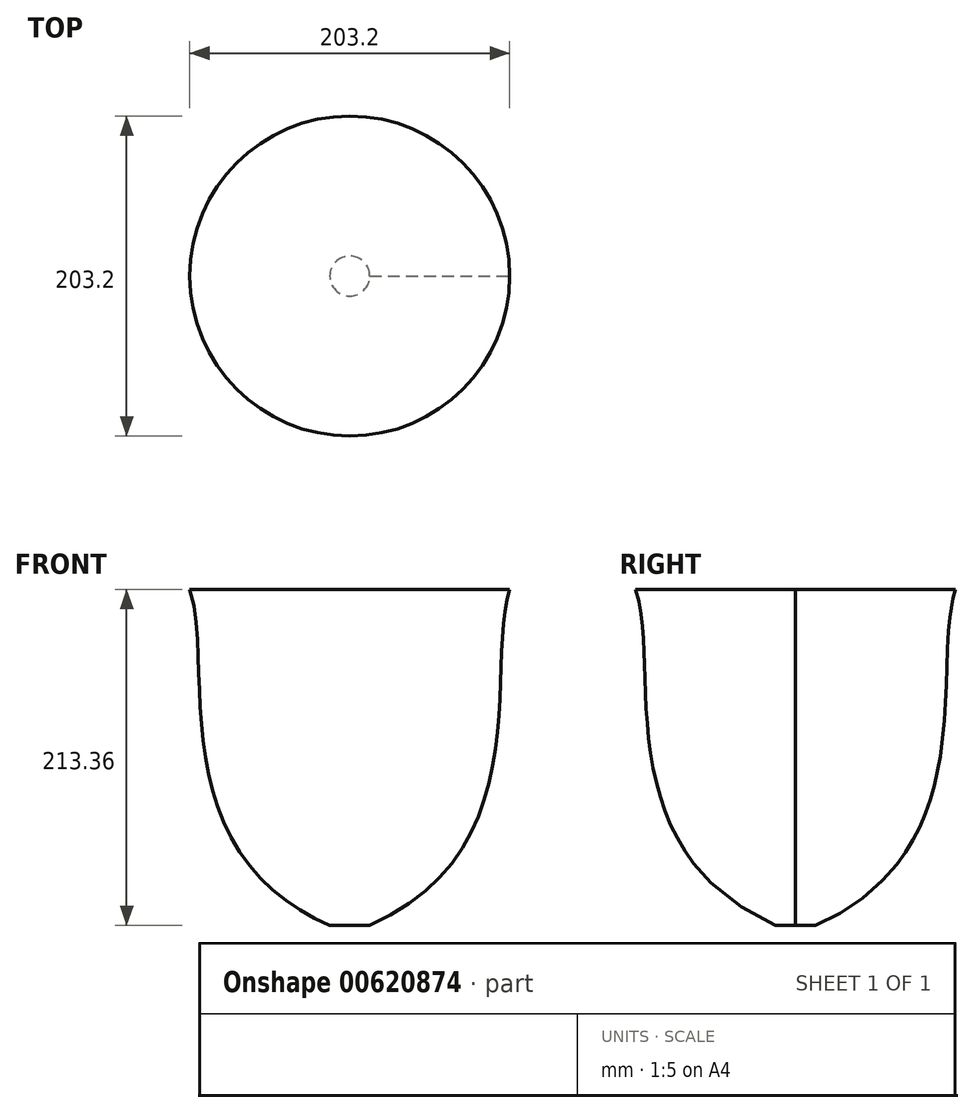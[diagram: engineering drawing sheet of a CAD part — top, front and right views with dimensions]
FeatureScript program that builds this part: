
annotation { "Feature Type Name" : "Feature", "Feature Type Description" : "" }
export const myFeature = defineFeature(function(context is Context, id is Id, definition is map)
    precondition{}
    {
        {
            var Q0;
            Q0=qCreatedBy(makeId("Front.planeOp"),FACE);
            var sketch = newSketch(context, id + "F0", { "sketchPlane" : qUnion([Q0])});
            skLineSegment(sketch, "E0.bottom", {"start": v(-101.6, 213.36) * mm, "end": v(101.6, 213.36) * mm, "construction": true});
            skLineSegment(sketch, "E0.top", {"start": v(-101.6, 0) * mm, "end": v(101.6, 0) * mm, "construction": true});
            skLineSegment(sketch, "E0.left", {"start": v(-101.6, 213.36) * mm, "end": v(-101.6, 0) * mm, "construction": true});
            skLineSegment(sketch, "E0.right", {"start": v(101.6, 213.36) * mm, "end": v(101.6, 0) * mm, "construction": true});
            skLineSegment(sketch, "E1", {"start": v(0, 33) * mm, "end": v(0, -35.39) * mm, "construction": true});
            skLineSegment(sketch, "E2", {"start": v(0, 0) * mm, "end": v(12.7, 0) * mm});
            skFitSpline(sketch, "E3", {"points": [v(12.7, 0) * mm, v(101.6, 213.36) * mm], "startDerivative": vector(324.37, 142.37) * mm, "endDerivative": vector(48.16, 142.84) * mm});
            skLineSegment(sketch, "E4", {"start": v(101.6, 213.36) * mm, "end": v(0, 213.36) * mm});
            skLineSegment(sketch, "E5", {"start": v(0, 213.36) * mm, "end": v(0, 0) * mm});
            skSolve(sketch);
        }
        {
            var Q0;
            Q0 = qSketchRegion(id + "F0", true);
            var Q1;
            Q1=sQuery(id+"F0.wireOp",EDGE,"E1");
            revolve(context, id + "F1", {"entities" : qUnion([Q0]), "axis" : qUnion([Q1]), "revolveType" : RevolveType.FULL});
        }
    });
